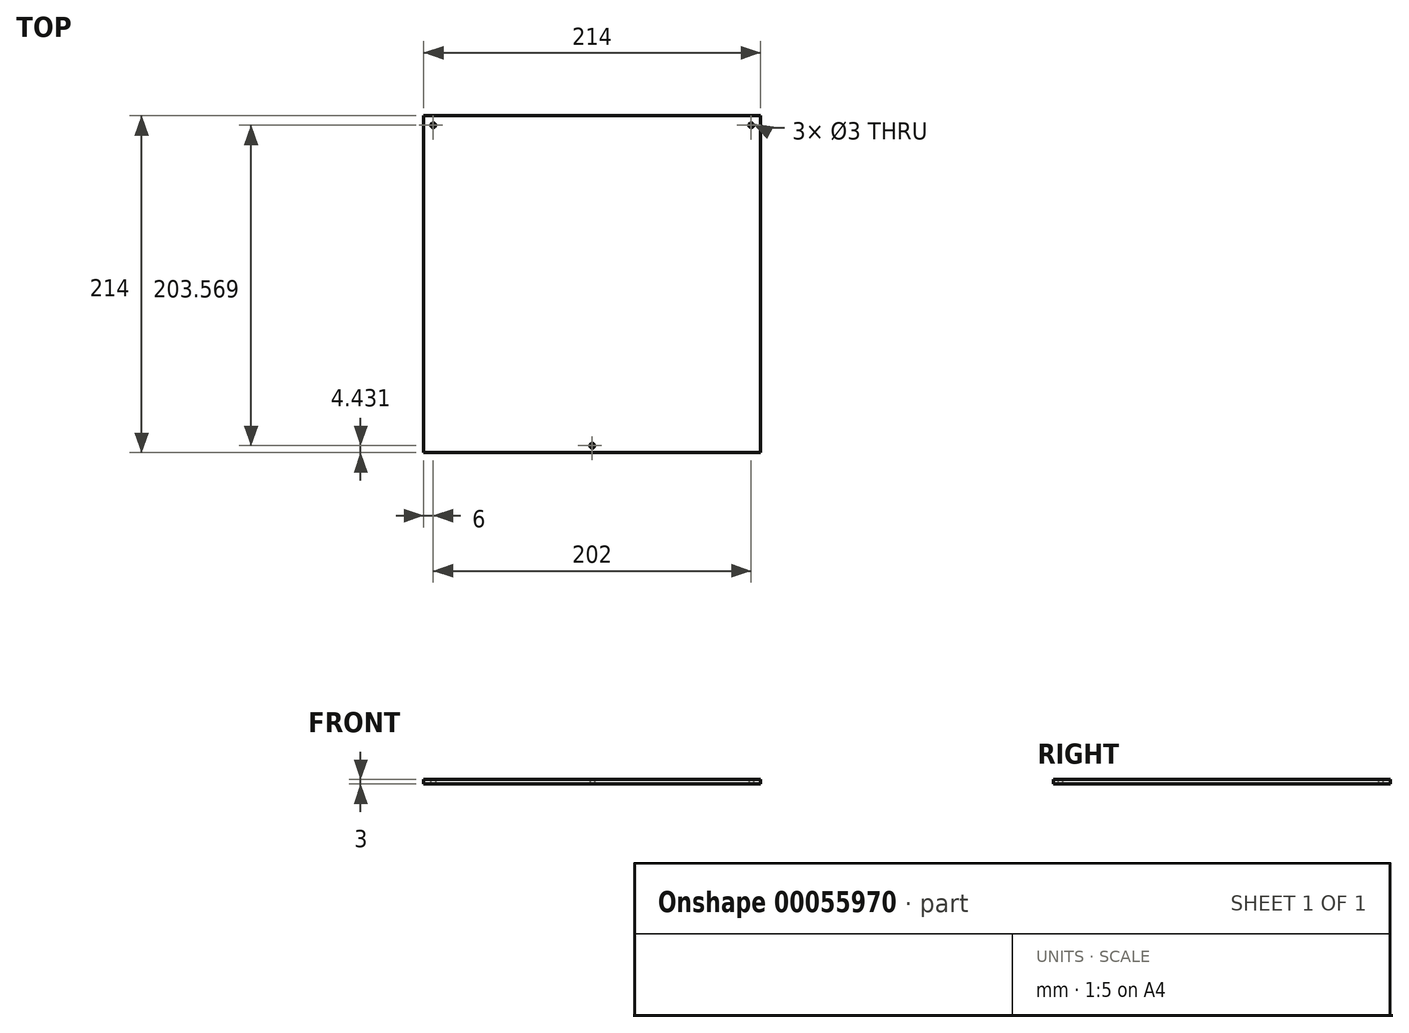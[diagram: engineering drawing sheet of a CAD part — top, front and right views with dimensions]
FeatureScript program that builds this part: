
annotation { "Feature Type Name" : "Feature", "Feature Type Description" : "" }
export const myFeature = defineFeature(function(context is Context, id is Id, definition is map)
    precondition{}
    {
        {
            var Q0;
            Q0=qCreatedBy(makeId("Top.planeOp"),FACE);
            var sketch = newSketch(context, id + "F0", { "sketchPlane" : qUnion([Q0])});
            skLineSegment(sketch, "E0.rect.bottom", {"start": v(107, 107) * mm, "end": v(-107, 107) * mm});
            skLineSegment(sketch, "E0.rect.top", {"start": v(107, -107) * mm, "end": v(-107, -107) * mm});
            skLineSegment(sketch, "E0.rect.left", {"start": v(107, 107) * mm, "end": v(107, -107) * mm});
            skLineSegment(sketch, "E0.rect.right", {"start": v(-107, 107) * mm, "end": v(-107, -107) * mm});
            skPoint(sketch, "E0.rect.middle", {"position": v(0, 0) * mm});
            skLineSegment(sketch, "E1", {"start": v(0, 0) * mm, "end": v(0, -102.57) * mm, "construction": true});
            skLineSegment(sketch, "E2.bottom", {"start": v(-107, 107) * mm, "end": v(-101, 107) * mm, "construction": true});
            skLineSegment(sketch, "E2.top", {"start": v(-107, 101) * mm, "end": v(-101, 101) * mm, "construction": true});
            skLineSegment(sketch, "E2.left", {"start": v(-107, 107) * mm, "end": v(-107, 101) * mm, "construction": true});
            skLineSegment(sketch, "E2.right", {"start": v(-101, 107) * mm, "end": v(-101, 101) * mm, "construction": true});
            skLineSegment(sketch, "E3.bottom", {"start": v(107, 107) * mm, "end": v(101, 107) * mm, "construction": true});
            skLineSegment(sketch, "E3.top", {"start": v(107, 101) * mm, "end": v(101, 101) * mm, "construction": true});
            skLineSegment(sketch, "E3.left", {"start": v(107, 107) * mm, "end": v(107, 101) * mm, "construction": true});
            skLineSegment(sketch, "E3.right", {"start": v(101, 107) * mm, "end": v(101, 101) * mm, "construction": true});
            skCircle(sketch, "E4", {"center": v(0, -102.57) * mm, "radius": 1.5 * mm});
            skCircle(sketch, "E5", {"center": v(-101, 101) * mm, "radius": 1.5 * mm});
            skCircle(sketch, "E6", {"center": v(101, 101) * mm, "radius": 1.5 * mm});
            skSolve(sketch);
        }
        {
            var Q0;
            Q0=makeQuery(id+"F0.imprint","IMPRINT",FACE,{"disambiguationData":[TD([[makeQuery(id+"F0.imprint","IMPRINT",EDGE,{"derivedFrom":sQuery(id+"F0.wireOp",EDGE,"E0.rect.bottom")}),1.0]])]});
            extrude(context, id + "F1", {"entities" : qUnion([Q0]), "depth" : 3 * mm});
        }
    });
